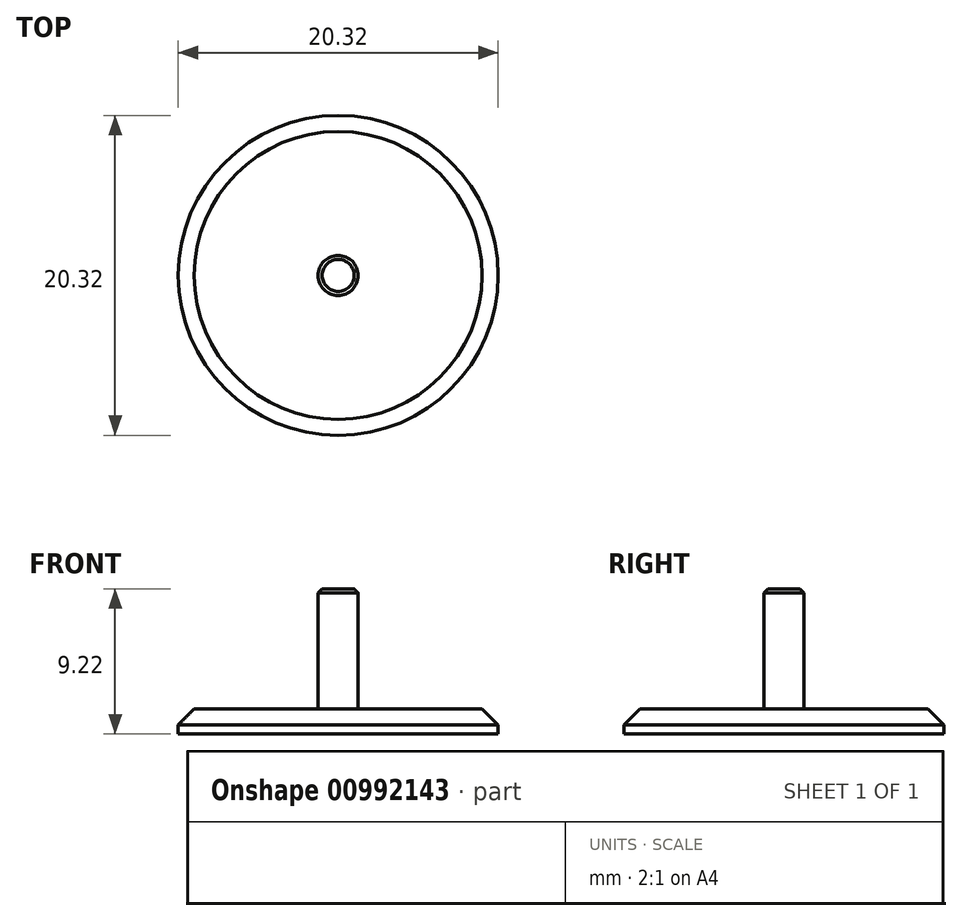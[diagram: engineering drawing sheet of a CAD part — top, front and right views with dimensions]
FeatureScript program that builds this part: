
annotation { "Feature Type Name" : "Feature", "Feature Type Description" : "" }
export const myFeature = defineFeature(function(context is Context, id is Id, definition is map)
    precondition{}
    {
        {
            var Q0;
            Q0=qCreatedBy(makeId("Top.planeOp"),FACE);
            var sketch = newSketch(context, id + "F0", { "sketchPlane" : qUnion([Q0])});
            skCircle(sketch, "E0", {"center": v(0, 0) * mm, "radius": 1.27 * mm});
            skSolve(sketch);
        }
        {
            var Q0;
            Q0 = qSketchRegion(id + "F0", true);
            extrude(context, id + "F1", {"entities" : qUnion([Q0]), "oppositeDirection" : true, "depth" : 7.62 * mm, "offsetDistance" : 25.4 * mm});
        }
        {
            var Q0;
            Q0=makeQuery(id+"F1.opExtrude","CAP_FACE",FACE,{"disambiguationData":[OSD([sQuery(id+"F0.wireOp",EDGE,"E0")])],"isStart":false});
            var sketch = newSketch(context, id + "F2", { "sketchPlane" : qUnion([Q0])});
            skCircle(sketch, "E1", {"center": v(0, 0) * mm, "radius": 10.16 * mm});
            skSolve(sketch);
        }
        {
            var Q0;
            Q0 = qSketchRegion(id + "F2", true);
            extrude(context, id + "F3", {"entities" : qUnion([Q0]), "operationType" : NewBodyOperationType.ADD, "depth" : 1.6 * mm, "offsetDistance" : 25.4 * mm});
        }
        {
            var Q0;
            Q0=makeQuery(id+"F3.opExtrude","CAP_EDGE",EDGE,{"disambiguationData":[OSD([sQuery(id+"F2.wireOp",EDGE,"E1")])],"isStart":true});
            chamfer(context, id + "F4", {"entities" : qUnion([Q0]), "width" : 1.02 * mm, "tangentPropagation" : true});
        }
        {
            var Q0;
            Q0=makeQuery(id+"F1.opExtrude","CAP_EDGE",EDGE,{"disambiguationData":[OSD([sQuery(id+"F0.wireOp",EDGE,"E0")])],"isStart":true});
            chamfer(context, id + "F5", {"entities" : qUnion([Q0]), "width" : 0.25 * mm, "tangentPropagation" : true});
        }
    });
